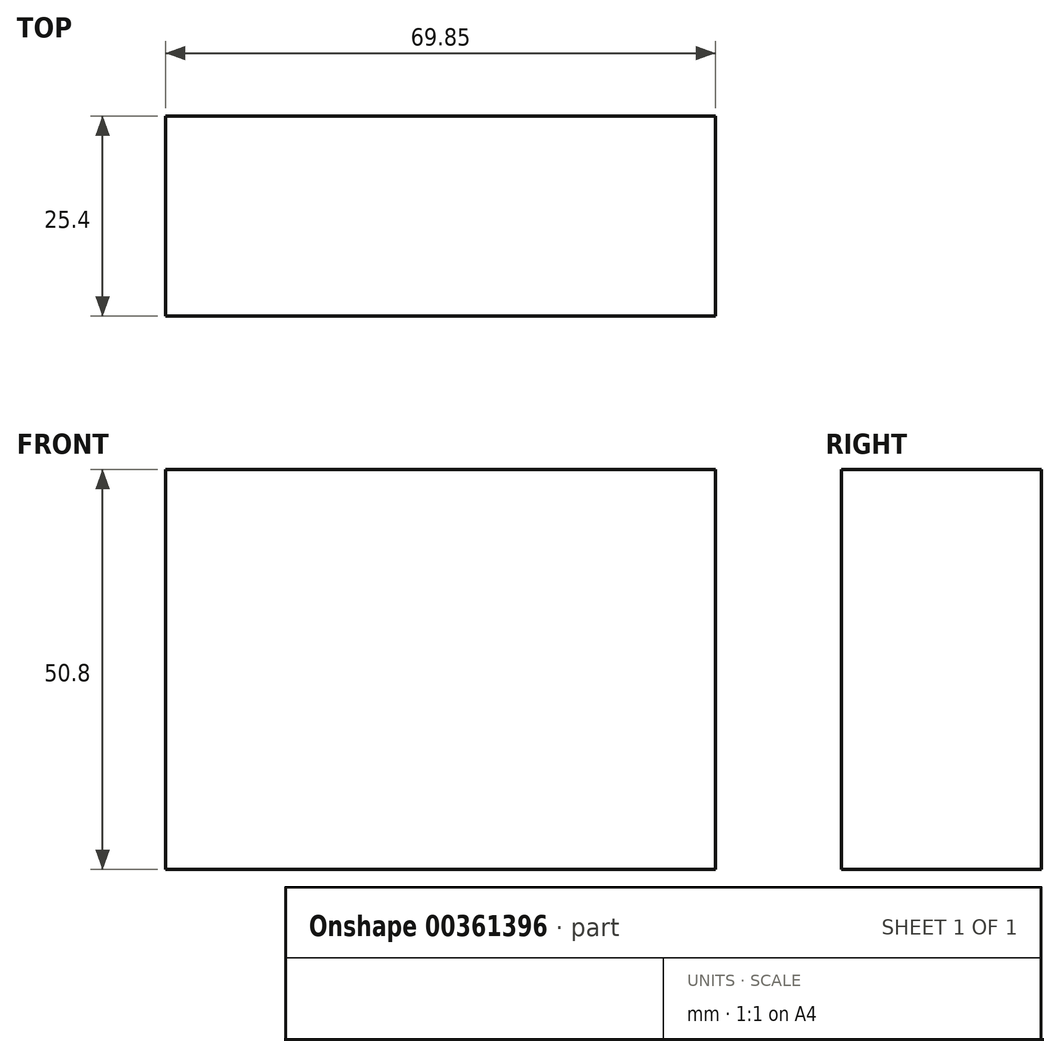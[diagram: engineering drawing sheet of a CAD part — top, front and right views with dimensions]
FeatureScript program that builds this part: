
annotation { "Feature Type Name" : "Feature", "Feature Type Description" : "" }
export const myFeature = defineFeature(function(context is Context, id is Id, definition is map)
    precondition{}
    {
        {
            var Q0;
            Q0=qCreatedBy(makeId("Front.planeOp"),FACE);
            var sketch = newSketch(context, id + "F0", { "sketchPlane" : qUnion([Q0])});
            skLineSegment(sketch, "E0.bottom", {"start": v(15.34, -17.35) * mm, "end": v(-54.5, -17.35) * mm});
            skLineSegment(sketch, "E0.top", {"start": v(15.34, 33.45) * mm, "end": v(-54.5, 33.45) * mm});
            skLineSegment(sketch, "E0.left", {"start": v(15.34, -17.35) * mm, "end": v(15.34, 33.45) * mm});
            skLineSegment(sketch, "E0.right", {"start": v(-54.5, -17.35) * mm, "end": v(-54.5, 33.45) * mm});
            skSolve(sketch);
        }
        {
            var Q0;
            Q0 = qSketchRegion(id + "F0", true);
            extrude(context, id + "F1", {"entities" : qUnion([Q0]), "depth" : 25.4 * mm});
        }
    });
